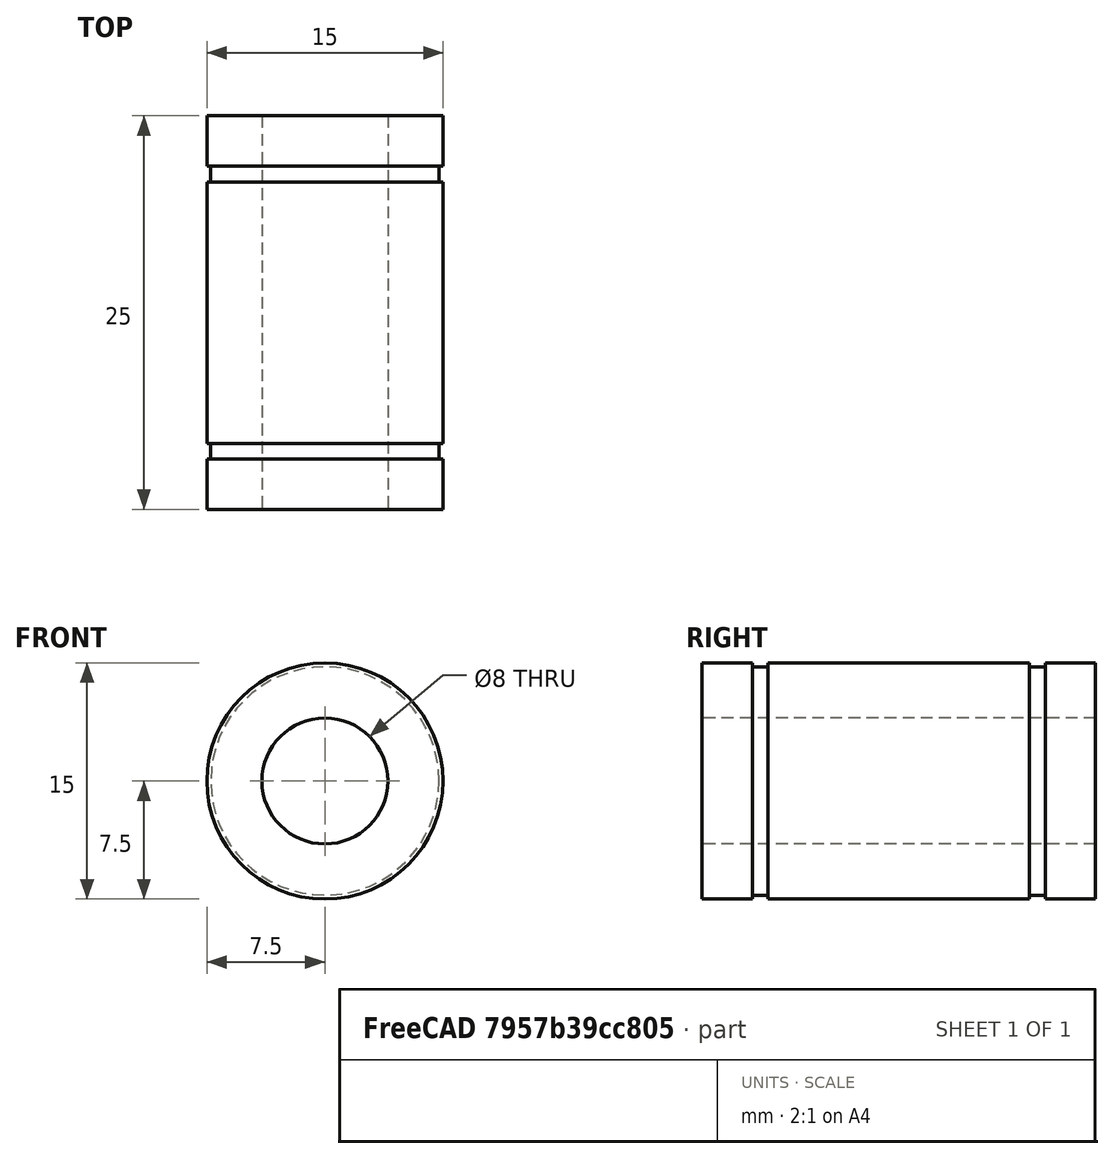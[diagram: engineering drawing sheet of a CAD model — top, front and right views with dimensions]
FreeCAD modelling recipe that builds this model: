
FCSTD DOCUMENT  (FreeCAD 0.18R)
Label: linear-bearing-lm8uu
License: All rights reserved
LicenseURL: http://en.wikipedia.org/wiki/All_rights_reserved
objects: Sketcher::SketchObject×1, PartDesign::Revolution×1, PartDesign::Body×1
note: 4 computed .brp shape members not serialized (recipe doc carries the construction recipe); baked Part::Feature solids carry a one-line shape summary decoded from their .brp

FEATURE [Sketcher::SketchObject] Sketch
  MapMode = 5
  Support = -> [XY_Plane]
  sketch-geometry (12):
    g0: LineSegment StartX=-7.5 StartY=25 StartZ=0 EndX=-4 EndY=25 EndZ=0
    g1: LineSegment StartX=-7.5 StartY=25 StartZ=0 EndX=-7.5 EndY=21.8 EndZ=0
    g2: LineSegment StartX=-7.5 StartY=0 StartZ=0 EndX=-4 EndY=0 EndZ=0
    g3: LineSegment StartX=-7.5 StartY=21.8 StartZ=0 EndX=-7.25 EndY=21.8 EndZ=0
    g4: LineSegment StartX=-7.25 StartY=21.8 StartZ=0 EndX=-7.25 EndY=20.8 EndZ=0
    g5: LineSegment StartX=-7.5 StartY=20.8 StartZ=0 EndX=-7.25 EndY=20.8 EndZ=0
    g6: LineSegment StartX=-7.5 StartY=3.2 StartZ=0 EndX=-7.25 EndY=3.2 EndZ=0
    g7: LineSegment StartX=-7.25 StartY=3.2 StartZ=0 EndX=-7.25 EndY=4.2 EndZ=0
    g8: LineSegment StartX=-7.5 StartY=3.2 StartZ=0 EndX=-7.5 EndY=0 EndZ=0
    g9: LineSegment StartX=-7.5 StartY=4.2 StartZ=0 EndX=-7.25 EndY=4.2 EndZ=0
    g10: LineSegment StartX=-7.5 StartY=20.8 StartZ=0 EndX=-7.5 EndY=4.2 EndZ=0
    g11: LineSegment StartX=-4 StartY=25 StartZ=0 EndX=-4 EndY=0 EndZ=0
  constraints (36):
    c: Horizontal(g0)
    c: Vertical(g1)
    c: PointOnObject(g2,g-1)
    c: PointOnObject(g2,g-1)
    c: Horizontal(g3)
    c: DistanceX(g0,g-1) = 4
    c: DistanceX(g0,g-1) = 7.5
    c: Coincident(g0,g1)
    c: DistanceY(g1,g1) = 3.2
    c: DistanceX(g3,g3) = 0.25
    c: Coincident(g1,g3)
    c: Coincident(g3,g4)
    c: Vertical(g4)
    c: DistanceY(g4,g4) = 1
    c: Coincident(g5,g4)
    c: Horizontal(g5)
    c: DistanceX(g5,g1) = 0
    c: Horizontal(g6)
    c: DistanceX(g6,g6) = 0.25
    c: Coincident(g6,g7)
    c: Vertical(g7)
    c: DistanceX(g2,g0) = 0
    c: DistanceX(g2,g6) = 0
    c: Coincident(g2,g8)
    c: DistanceY(g-1,g0) = 25
    c: Horizontal(g9)
    c: Coincident(g7,g9)
    c: Coincident(g10,g5)
    c: Coincident(g10,g9)
    c: Vertical(g10)
    c: Coincident(g6,g8)
    c: DistanceY(g7,g7) = 1
    c: DistanceY(g8,g8) = 3.2
    c: DistanceX(g9,g6) = 0
    c: Coincident(g11,g2)
    c: Coincident(g0,g11)
FEATURE [PartDesign::Revolution] Revolution
  Angle = 360
  Axis = (0,1,0)
  Base = (0,0,0)
  Profile = -> Sketch
  ReferenceAxis = -> Sketch [V_Axis]
FEATURE [PartDesign::Body] Body  label="linear-bearing-lm8uu"
  Group = -> [Sketch,Revolution]
  Origin = -> Origin
  Tip = -> Revolution
